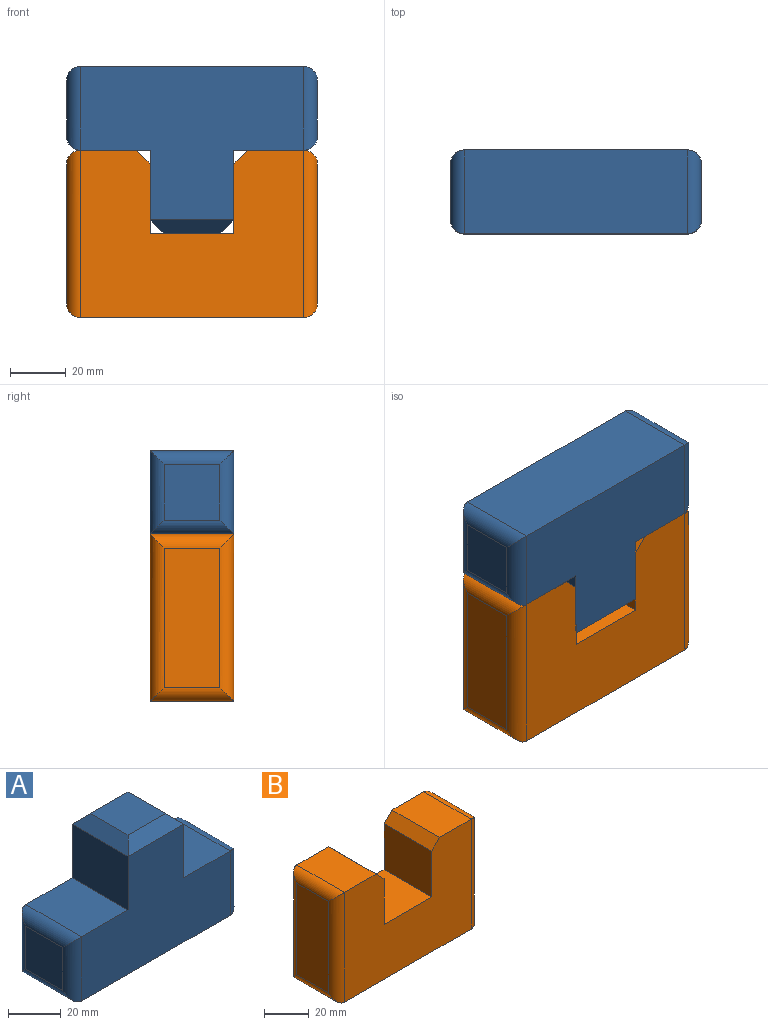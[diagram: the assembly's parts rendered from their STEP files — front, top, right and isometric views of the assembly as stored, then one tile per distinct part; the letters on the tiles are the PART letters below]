
ASSEMBLY  parts=2 mates=1
PART A: 22 faces, bbox 90x30x60 mm
  f0: plane 30x25mm, normal (0,0,1), area 750mm2, adj f1,f3,f8,f19
  f1: plane 80x55mm, normal (0,-1,0), area 3150mm2, adj f0,f5,f6,f7,f8,f10,f17,f18
  f2: plane 20x20mm, normal (1,0,0), area 400mm2, adj f14,f15,f16,f17
  f3: plane 80x55mm, normal (0,1,0), area 3150mm2, adj f0,f5,f6,f7,f8,f13,f14,f21
  f4: plane 20x20mm, normal (-1,0,0), area 400mm2, adj f18,f19,f20,f21
  f5: plane 30x25mm, normal (0,0,1), area 750mm2, adj f1,f3,f7,f15
  f6: plane 80x30mm, normal (0,0,-1), area 2400mm2, adj f1,f3,f16,f20
  f7: plane 30x25mm, normal (1,0,0), area 750mm2, adj f1,f3,f5,f11
  f8: plane 30x25mm, normal (-1,0,0), area 750mm2, adj f0,f1,f3,f12
  f9: plane 20x20mm, normal (0,0,1), area 400mm2, adj f10,f11,f12,f13
  f10: plane 30x5mm, normal (0,-0.71,0.71), area 176.8mm2, adj f1,f9,f11,f12
  f11: plane 30x5mm, normal (0.71,0,0.71), area 176.8mm2, adj f7,f9,f10,f13
  f12: plane 30x5mm, normal (-0.71,0,0.71), area 176.8mm2, adj f8,f9,f10,f13
  f13: plane 30x5mm, normal (0,0.71,0.71), area 176.8mm2, adj f3,f9,f11,f12
  f14: cylinder r=5mm len=30mm, axis (0,0,-1), area 207.1mm2, adj f2,f3,f15,f16
  f15: cylinder r=5mm len=30mm, axis (0,-1,0), area 207.1mm2, adj f2,f5,f14,f17
  f16: cylinder r=5mm len=30mm, axis (0,1,0), area 207.1mm2, adj f2,f6,f14,f17
  f17: cylinder r=5mm len=30mm, axis (0,0,1), area 207.1mm2, adj f1,f2,f15,f16
  f18: cylinder r=5mm len=30mm, axis (0,0,-1), area 207.1mm2, adj f1,f4,f19,f20
  f19: cylinder r=5mm len=30mm, axis (0,1,0), area 207.1mm2, adj f0,f4,f18,f21
  f20: cylinder r=5mm len=30mm, axis (0,-1,0), area 207.1mm2, adj f4,f6,f18,f21
  f21: cylinder r=5mm len=30mm, axis (0,0,1), area 207.1mm2, adj f3,f4,f19,f20
PART B: 20 faces, bbox 90x30x60 mm
  f0: plane 30x20mm, normal (0,0,1), area 600mm2, adj f1,f3,f11,f17
  f1: plane 80x60mm, normal (0,-1,0), area 3875mm2, adj f0,f5,f6,f7,f8,f9,f10,f11
  f2: plane 50x20mm, normal (1,0,0), area 1000mm2, adj f12,f13,f14,f15
  f3: plane 80x60mm, normal (0,1,0), area 3875mm2, adj f0,f5,f6,f7,f8,f9,f10,f11
  f4: plane 50x20mm, normal (-1,0,0), area 1000mm2, adj f16,f17,f18,f19
  f5: plane 30x20mm, normal (0,0,1), area 600mm2, adj f1,f3,f10,f13
  f6: plane 80x30mm, normal (0,0,-1), area 2400mm2, adj f1,f3,f14,f18
  f7: plane 30x25mm, normal (-1,0,0), area 750mm2, adj f1,f3,f9,f10
  f8: plane 30x25mm, normal (1,0,0), area 750mm2, adj f1,f3,f9,f11
  f9: plane 30x30mm, normal (0,0,1), area 900mm2, adj f1,f3,f7,f8
  f10: plane 30x5mm, normal (-0.71,0,0.71), area 212.1mm2, adj f1,f3,f5,f7
  f11: plane 30x5mm, normal (0.71,0,0.71), area 212.1mm2, adj f0,f1,f3,f8
  f12: cylinder r=5mm len=60mm, axis (0,0,-1), area 442.7mm2, adj f2,f3,f13,f14
  f13: cylinder r=5mm len=30mm, axis (0,-1,0), area 207.1mm2, adj f2,f5,f12,f15
  f14: cylinder r=5mm len=30mm, axis (0,1,0), area 207.1mm2, adj f2,f6,f12,f15
  f15: cylinder r=5mm len=60mm, axis (0,0,1), area 442.7mm2, adj f1,f2,f13,f14
  f16: cylinder r=5mm len=60mm, axis (0,0,-1), area 442.7mm2, adj f1,f4,f17,f18
  f17: cylinder r=5mm len=30mm, axis (0,1,0), area 207.1mm2, adj f0,f4,f16,f19
  f18: cylinder r=5mm len=30mm, axis (0,-1,0), area 207.1mm2, adj f4,f6,f16,f19
  f19: cylinder r=5mm len=60mm, axis (0,0,1), area 442.7mm2, adj f3,f4,f17,f18
PLACE A rot(axis=(1,0,0),180deg) t=(-3.78,12.94,27.39)mm
PLACE B t=(-3.78,-28.17,-62.61)mm fixed
MATE fastened B.f9 <-> A.f9  axis (0,0,1) through (-3.78,12.94,-32.61)mm
